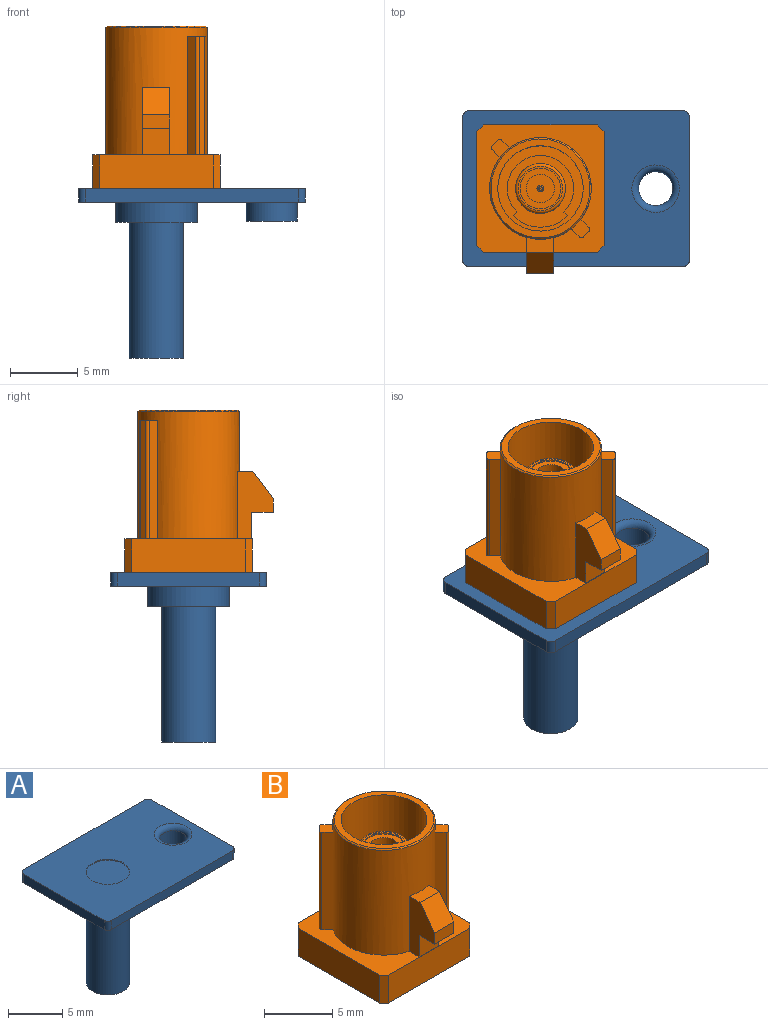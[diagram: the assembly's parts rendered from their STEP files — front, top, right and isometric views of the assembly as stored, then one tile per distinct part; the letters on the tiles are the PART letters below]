
ASSEMBLY  parts=2 mates=1
PART A: 20 faces, bbox 16.8x11.5x12.5 mm
  f0: plane 15.75x1mm, normal (0,1,0), area 15.8mm2, adj f5,f6,f7,f10
  f1: plane 10.5x1mm, normal (-1,0,0), area 10.5mm2, adj f5,f6,f7,f8
  f2: plane 15.75x1mm, normal (0,-1,0), area 15.8mm2, adj f5,f6,f8,f9
  f3: cylinder r=1.25mm len=2.5mm, axis (0,0,1), area 14.9mm2, adj f12,f17
  f4: plane 10.5x1mm, normal (1,0,0), area 10.5mm2, adj f5,f6,f9,f10
  f5: plane 16.75x11.5mm, normal (0,0,-1), area 153.1mm2, adj f0,f1,f2,f4,f7,f8,f9,f10
  f6: plane 16.75x11.5mm, normal (0,0,1), area 170.2mm2, adj f0,f1,f2,f4,f7,f8,f9,f10
  f7: cylinder r=0.5mm len=1mm, axis (0,0,-1), area 0.8mm2, adj f0,f1,f5,f6
  f8: cylinder r=0.5mm len=1mm, axis (0,0,1), area 0.8mm2, adj f1,f2,f5,f6
  f9: cylinder r=0.5mm len=1mm, axis (0,0,-1), area 0.8mm2, adj f2,f4,f5,f6
  f10: cylinder r=0.5mm len=1mm, axis (0,0,1), area 0.8mm2, adj f0,f4,f5,f6
  f11: cylinder r=1.88mm len=3.75mm, axis (0,0,1), area 16.5mm2, adj f5,f12
  f12: plane 3.75x3.75mm, normal (0,0,-1), area 6.1mm2, adj f3,f11
  f13: cylinder r=3mm len=6mm, axis (0,0,1), area 28.3mm2, adj f5,f14
  f14: plane 6x6mm, normal (0,0,-1), area 15.7mm2, adj f13,f16
  f15: plane 4x4mm, normal (0,0,-1), area 12.6mm2, adj f16
  f16: cylinder r=2mm len=10mm, axis (0,0,1), area 125.7mm2, adj f14,f15
  f17: torus R=1.75mm, axis (0,0,1), area 7.1mm2, adj f3,f6
  f18: cylinder r=2mm len=4mm, axis (0,0,1), area 1.3mm2, adj f6,f19
  f19: plane 4x4mm, normal (0,0,1), area 12.6mm2, adj f18
PART B: 70 faces, bbox 9.4x10.9x12 mm
  f0: cylinder r=3mm len=6mm, axis (0,0,-1), area 35.6mm2, adj f1,f7,f18,f22,f23,f24,f26
  f1: plane 2.48x0.62mm, normal (0,0,1), area 0.9mm2, adj f0,f18,f19,f20,f21,f22,f23,f24
  f2: plane 9.4x9.4mm, normal (0,0,1), area 39.8mm2, adj f3,f4,f5,f6,f8,f9,f10,f11
  f3: plane 8.4x2.5mm, normal (0,-1,0), area 21mm2, adj f2,f7,f8,f11
  f4: plane 8.4x2.5mm, normal (1,0,0), area 21mm2, adj f2,f7,f8,f9
  f5: plane 8.4x2.5mm, normal (0,1,0), area 21mm2, adj f2,f7,f9,f10
  f6: plane 8.4x2.5mm, normal (-1,0,0), area 21mm2, adj f2,f7,f10,f11
  f7: plane 9.4x9.4mm, normal (0,0,-1), area 59.6mm2, adj f0,f3,f4,f5,f6,f8,f9,f10
  f8: plane 2.5x0.5mm, normal (0.71,-0.71,0), area 1.8mm2, adj f2,f3,f4,f7
  f9: plane 2.5x0.5mm, normal (0.71,0.71,0), area 1.8mm2, adj f2,f4,f5,f7
  f10: plane 2.5x0.5mm, normal (-0.71,0.71,0), area 1.8mm2, adj f2,f5,f6,f7
  f11: plane 2.5x0.5mm, normal (-0.71,-0.71,0), area 1.8mm2, adj f2,f3,f6,f7
  f12: plane 2.48x0.73mm, normal (0,0,-1), area 0.5mm2, adj f13,f14,f15,f16,f17,f18,f19,f20
  f13: cylinder r=0.2mm len=1.88mm, axis (-1,0,0), area 0.5mm2, adj f12,f15,f16,f25
  f14: cylinder r=2.9mm len=1.65mm, axis (0,0,-1), area 0.9mm2, adj f12,f15,f22,f23,f26
  f15: cylinder r=0.2mm len=0.51mm, axis (0,1,0), area 0.1mm2, adj f12,f13,f14,f23
  f16: cylinder r=0.2mm len=0.51mm, axis (0,-1,0), area 0.1mm2, adj f12,f13,f17,f24
  f17: cylinder r=2.9mm len=1.65mm, axis (0,0,-1), area 0.9mm2, adj f12,f16,f18,f24,f26
  f18: plane 1.65x0.43mm, normal (-1,0,0), area 0.5mm2, adj f0,f1,f12,f17,f19,f26
  f19: cylinder r=0.3mm len=1mm, axis (0,0,1), area 0.5mm2, adj f1,f12,f18,f20
  f20: plane 1.88x1mm, normal (0,1,0), area 1.9mm2, adj f1,f12,f19,f21
  f21: cylinder r=0.3mm len=1mm, axis (0,0,1), area 0.5mm2, adj f1,f12,f20,f22
  f22: plane 1.65x0.43mm, normal (1,0,0), area 0.5mm2, adj f0,f1,f12,f14,f21,f26
  f23: plane 1.45x0.25mm, normal (-1,0,0), area 0.3mm2, adj f0,f1,f14,f15,f25,f26
  f24: plane 1.45x0.25mm, normal (1,0,0), area 0.3mm2, adj f0,f1,f16,f17,f25,f26
  f25: plane 1.48x0.8mm, normal (0,-1,0), area 1.2mm2, adj f1,f13,f23,f24
  f26: plane 6x6mm, normal (0,0,-1), area 28.2mm2, adj f0,f14,f17,f18,f22,f23,f24
  f27: plane 2x1.95mm, normal (0,-1,0), area 3.9mm2, adj f2,f28,f61,f62
  f28: plane 4.95x2.63mm, normal (1,0,0), area 8.4mm2, adj f2,f27,f29,f62,f63,f64,f65
  f29: cylinder r=3.75mm len=9.4mm, axis (0,0,-1), area 193.9mm2, adj f2,f28,f30,f31,f32,f33,f34,f38
  f30: plane 1.36x1.36mm, normal (0,0,1), area 1mm2, adj f29,f31,f66,f67,f68,f69
  f31: plane 8.71x0.59mm, normal (0.71,0.71,0), area 7.3mm2, adj f2,f29,f30,f69
  f32: plane 8.71x0.59mm, normal (0.71,0.71,0), area 7.3mm2, adj f2,f29,f33,f37
  f33: plane 1.36x1.36mm, normal (0,0,1), area 1mm2, adj f29,f32,f34,f35,f36,f37
  f34: plane 8.71x0.59mm, normal (-0.71,-0.71,0), area 7.3mm2, adj f2,f29,f33,f35
  f35: cylinder r=0.2mm len=8.71mm, axis (0,0,1), area 2.7mm2, adj f2,f33,f34,f36
  f36: plane 8.71x0.42mm, normal (-0.71,0.71,0), area 5.2mm2, adj f2,f33,f35,f37
  f37: cylinder r=0.2mm len=8.71mm, axis (0,0,1), area 2.7mm2, adj f2,f32,f33,f36
  f38: cone r=3.7mm half-angle=45deg, axis (0,0,-1), area 3.3mm2, adj f29,f39
  f39: plane 7.3x7.3mm, normal (0,0,1), area 10.6mm2, adj f38,f40
  f40: cylinder r=3.15mm len=7.55mm, axis (0,0,1), area 149.4mm2, adj f39,f41
  f41: plane 6.3x6.3mm, normal (0,0,1), area 10.7mm2, adj f40,f42,f43,f45,f46
  f42: cylinder r=2.45mm len=4.9mm, axis (0,0,1), area 5.8mm2, adj f41,f43,f44,f46
  f43: plane 0.5x0.28mm, normal (-0.71,-0.71,0), area 0.2mm2, adj f41,f42,f44,f45
  f44: plane 5.3x4.9mm, normal (0,0,1), area 9.9mm2, adj f42,f43,f45,f46,f47
  f45: cylinder r=2.85mm len=4.03mm, axis (0,0,1), area 2.2mm2, adj f41,f43,f44,f46
  f46: plane 0.5x0.28mm, normal (0.71,-0.71,0), area 0.2mm2, adj f41,f42,f44,f45
  f47: cylinder r=1.84mm len=5.61mm, axis (0,0,1), area 64.9mm2, adj f44,f48
  f48: torus R=1.64mm, axis (0,0,1), area 3.5mm2, adj f47,f49
  f49: plane 3.28x3.28mm, normal (0,0,1), area 1.4mm2, adj f48,f50
  f50: cylinder r=1.5mm len=3mm, axis (0,0,1), area 1mm2, adj f49,f51
  f51: plane 3x3mm, normal (0,0,1), area 3.6mm2, adj f50,f52
  f52: cylinder r=1.05mm len=3.43mm, axis (0,0,1), area 22.6mm2, adj f51,f53
  f53: plane 2.1x2.1mm, normal (0,0,1), area 3.3mm2, adj f52,f54,f58,f59,f60
  f54: cylinder r=0.05mm len=2.43mm, axis (0,0,-1), area 0.8mm2, adj f53,f55,f58,f60
  f55: cone r=0.03mm half-angle=6.8deg, axis (0,0,-1), area 0.1mm2, adj f54,f56,f58,f60
  f56: plane 0.25x0.25mm, normal (0,0,1), area 0mm2, adj f55,f57,f58,f60
  f57: cone r=0.19mm half-angle=18.5deg, axis (0,0,-1), area 0.5mm2, adj f56,f58,f59,f60
  f58: plane 2.85x0.26mm, normal (0,-1,0), area 0.6mm2, adj f53,f54,f55,f56,f57,f59
  f59: cylinder r=0.25mm len=2.46mm, axis (0,0,1), area 3.9mm2, adj f53,f57,f58,f60
  f60: plane 2.85x0.25mm, normal (0,1,0), area 0.6mm2, adj f53,f54,f55,f56,f57,f59
  f61: plane 4.95x2.63mm, normal (-1,0,0), area 8.4mm2, adj f2,f27,f29,f62,f63,f64,f65
  f62: plane 2x1.6mm, normal (0,0,-1), area 3.2mm2, adj f27,f28,f61,f63
  f63: plane 2x0.99mm, normal (0,-1,0), area 2mm2, adj f28,f61,f62,f64
  f64: plane 2.01x2mm, normal (0,-0.8,0.6), area 5mm2, adj f28,f61,f63,f65
  f65: plane 2x1.14mm, normal (0,0,1), area 2.1mm2, adj f28,f29,f61,f64
  f66: plane 8.71x0.59mm, normal (-0.71,-0.71,0), area 7.3mm2, adj f2,f29,f30,f67
  f67: cylinder r=0.2mm len=8.71mm, axis (0,0,1), area 2.7mm2, adj f2,f30,f66,f68
  f68: plane 8.71x0.42mm, normal (0.71,-0.71,0), area 5.2mm2, adj f2,f30,f67,f69
  f69: cylinder r=0.2mm len=8.71mm, axis (0,0,1), area 2.7mm2, adj f2,f30,f31,f68
PLACE A at identity
PLACE B at identity
MATE fastened B.f0 <-> A.f16  axis (0,0,-1) through (0,0,0)mm
